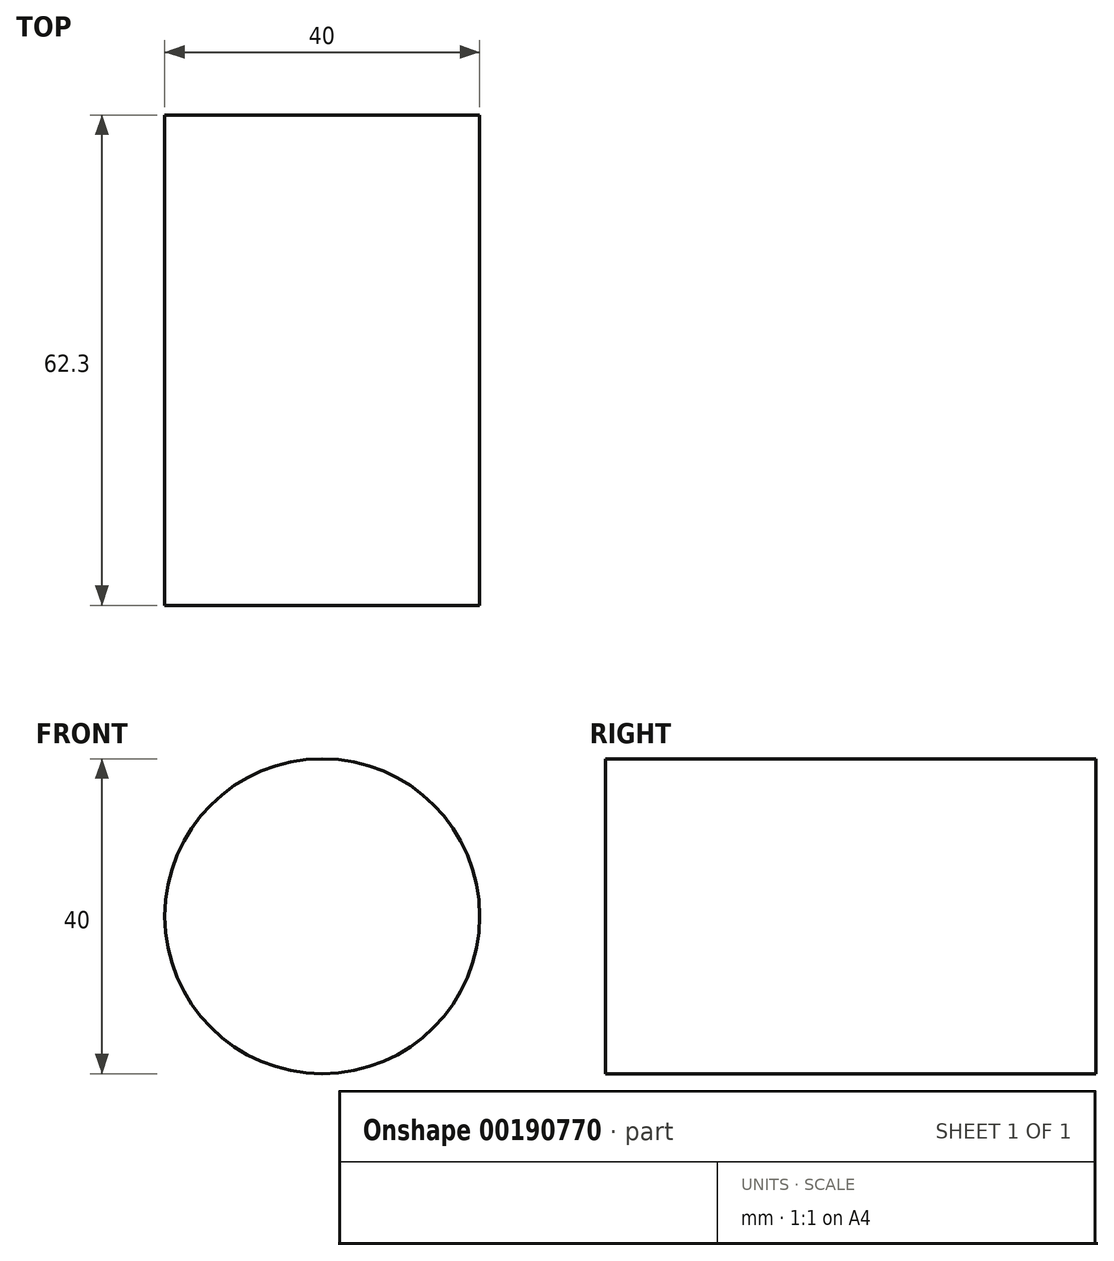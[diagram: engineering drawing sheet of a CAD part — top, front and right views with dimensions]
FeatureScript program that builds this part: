
annotation { "Feature Type Name" : "Feature", "Feature Type Description" : "" }
export const myFeature = defineFeature(function(context is Context, id is Id, definition is map)
    precondition{}
    {
        {
            var Q0;
            Q0=qCreatedBy(makeId("Front.planeOp"),FACE);
            var sketch = newSketch(context, id + "F0", { "sketchPlane" : qUnion([Q0])});
            skCircle(sketch, "E0", {"center": v(0, 0) * mm, "radius": 20 * mm});
            skSolve(sketch);
        }
        {
            var Q0;
            Q0 = qSketchRegion(id + "F0", true);
            extrude(context, id + "F1", {"entities" : qUnion([Q0]), "depth" : 62.3 * mm});
        }
    });
